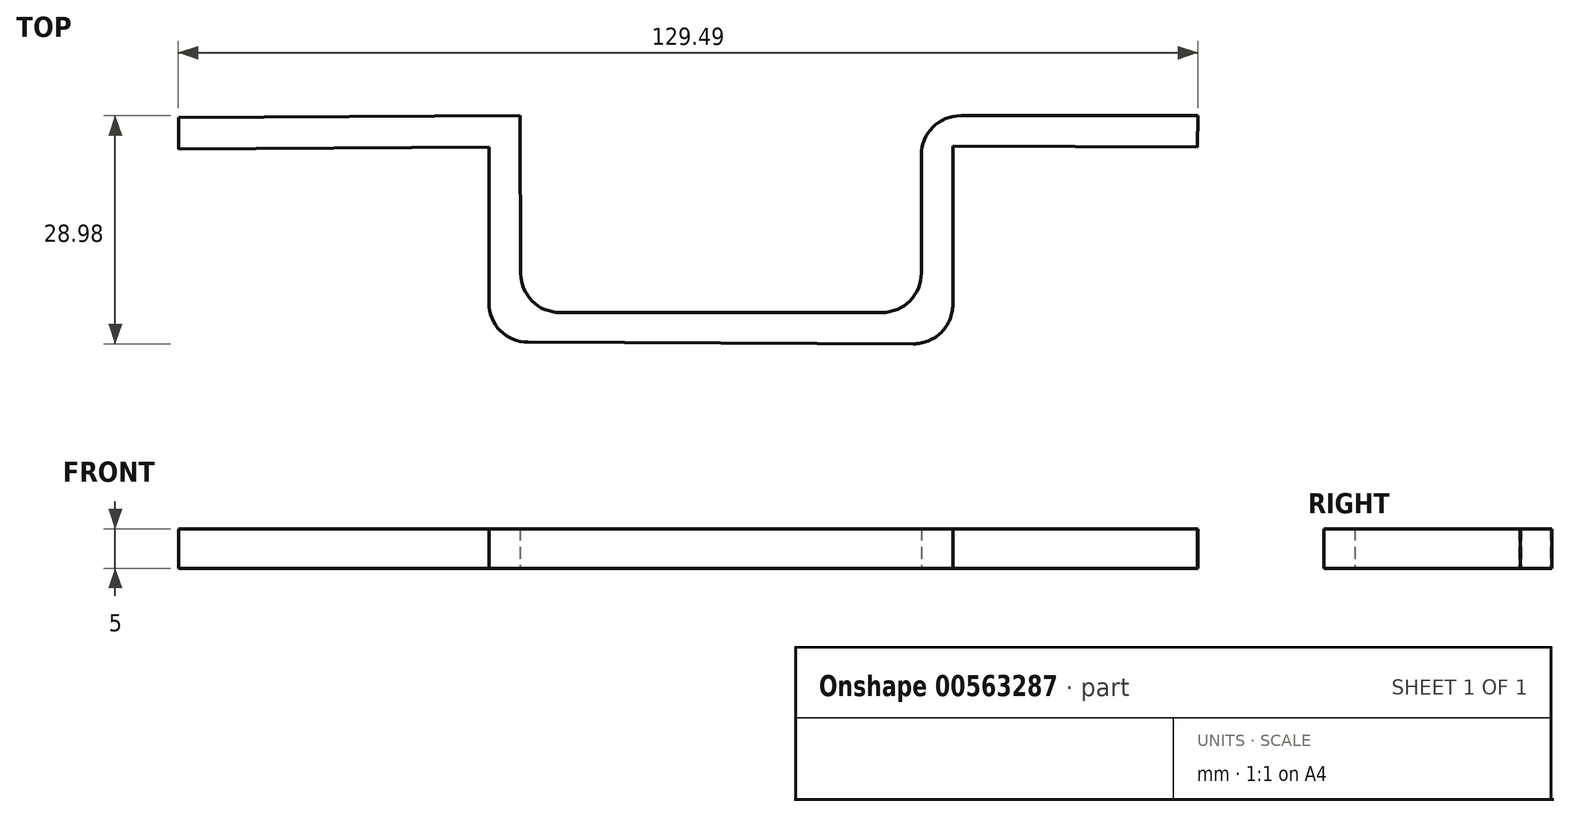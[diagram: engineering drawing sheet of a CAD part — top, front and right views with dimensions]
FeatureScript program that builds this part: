
annotation { "Feature Type Name" : "Feature", "Feature Type Description" : "" }
export const myFeature = defineFeature(function(context is Context, id is Id, definition is map)
    precondition{}
    {
        {
            var Q0;
            Q0=qCreatedBy(makeId("Top.planeOp"),FACE);
            var sketch = newSketch(context, id + "F0", { "sketchPlane" : qUnion([Q0])});
            skLineSegment(sketch, "E0", {"start": v(57.34, 14.56) * mm, "end": v(27.27, 14.56) * mm});
            skLineSegment(sketch, "E1", {"start": v(57.34, 14.56) * mm, "end": v(27.23, 14.56) * mm});
            skLineSegment(sketch, "E2", {"start": v(22.23, 9.56) * mm, "end": v(22.23, -5.44) * mm});
            skLineSegment(sketch, "E3", {"start": v(17.23, -10.44) * mm, "end": v(-23.67, -10.44) * mm});
            skLineSegment(sketch, "E4", {"start": v(-28.67, -5.46) * mm, "end": v(-28.77, 14.56) * mm});
            skLineSegment(sketch, "E5", {"start": v(-28.77, 14.56) * mm, "end": v(-72.15, 14.35) * mm});
            skLineSegment(sketch, "E6", {"start": v(-72.15, 14.35) * mm, "end": v(-72.13, 10.35) * mm});
            skLineSegment(sketch, "E7", {"start": v(-3.2, -14.31) * mm, "end": v(-3.2, -14.44) * mm});
            skLineSegment(sketch, "E8", {"start": v(57.34, 14.56) * mm, "end": v(57.33, 10.56) * mm});
            skLineSegment(sketch, "E9", {"start": v(57.33, 10.56) * mm, "end": v(26.23, 10.7) * mm});
            skLineSegment(sketch, "E10", {"start": v(26.23, 10.7) * mm, "end": v(26.23, -9.42) * mm});
            skLineSegment(sketch, "E11", {"start": v(21.2, -14.42) * mm, "end": v(-27.73, -14.21) * mm});
            skLineSegment(sketch, "E12", {"start": v(-32.7, -9.21) * mm, "end": v(-32.7, 10.56) * mm});
            skLineSegment(sketch, "E13", {"start": v(-32.7, 10.56) * mm, "end": v(-72.13, 10.35) * mm});
            skPoint(sketch, "E14.visualSharp", {"position": v(22.23, -10.44) * mm});
            skArc(sketch, "E14.filletArc", {"start": v(17.23, -10.44) * mm, "mid": v(20.77, -8.97) * mm, "end": v(22.23, -5.44) * mm});
            skPoint(sketch, "E15.visualSharp", {"position": v(-28.65, -10.44) * mm});
            skArc(sketch, "E15.filletArc", {"start": v(-28.67, -5.46) * mm, "mid": v(-27.2, -8.98) * mm, "end": v(-23.67, -10.44) * mm});
            skPoint(sketch, "E16.visualSharp", {"position": v(22.23, 14.56) * mm});
            skArc(sketch, "E16.filletArc", {"start": v(27.23, 14.56) * mm, "mid": v(23.7, 13.1) * mm, "end": v(22.23, 9.56) * mm});
            skPoint(sketch, "E17.visualSharp", {"position": v(26.23, -14.44) * mm});
            skArc(sketch, "E17.filletArc", {"start": v(21.2, -14.42) * mm, "mid": v(24.76, -12.96) * mm, "end": v(26.23, -9.42) * mm});
            skPoint(sketch, "E18.visualSharp", {"position": v(-32.7, -14.19) * mm});
            skArc(sketch, "E18.filletArc", {"start": v(-32.7, -9.21) * mm, "mid": v(-31.25, -12.74) * mm, "end": v(-27.73, -14.21) * mm});
            skPoint(sketch, "E19.end.orphan", {"position": v(-32.7, 2.06) * mm});
            skPoint(sketch, "E19.start.orphan", {"position": v(-28.7, 2.06) * mm});
            skPoint(sketch, "E20.orphan", {"position": v(-3.2, -10.44) * mm});
            skPoint(sketch, "E21.end.orphan", {"position": v(26.23, 2.06) * mm});
            skPoint(sketch, "E21.start.orphan", {"position": v(22.23, 2.06) * mm});
            skSolve(sketch);
        }
        {
            var Q0;
            Q0=makeQuery(id+"F0.imprint","IMPRINT",FACE,{"disambiguationData":[TD([[makeQuery(id+"F0.imprint","IMPRINT",EDGE,{"derivedFrom":sQuery(id+"F0.wireOp",EDGE,"E2")}),1.0]])]});
            extrude(context, id + "F1", {"entities" : qUnion([Q0]), "depth" : 5 * mm, "offsetDistance" : 25 * mm});
        }
    });
